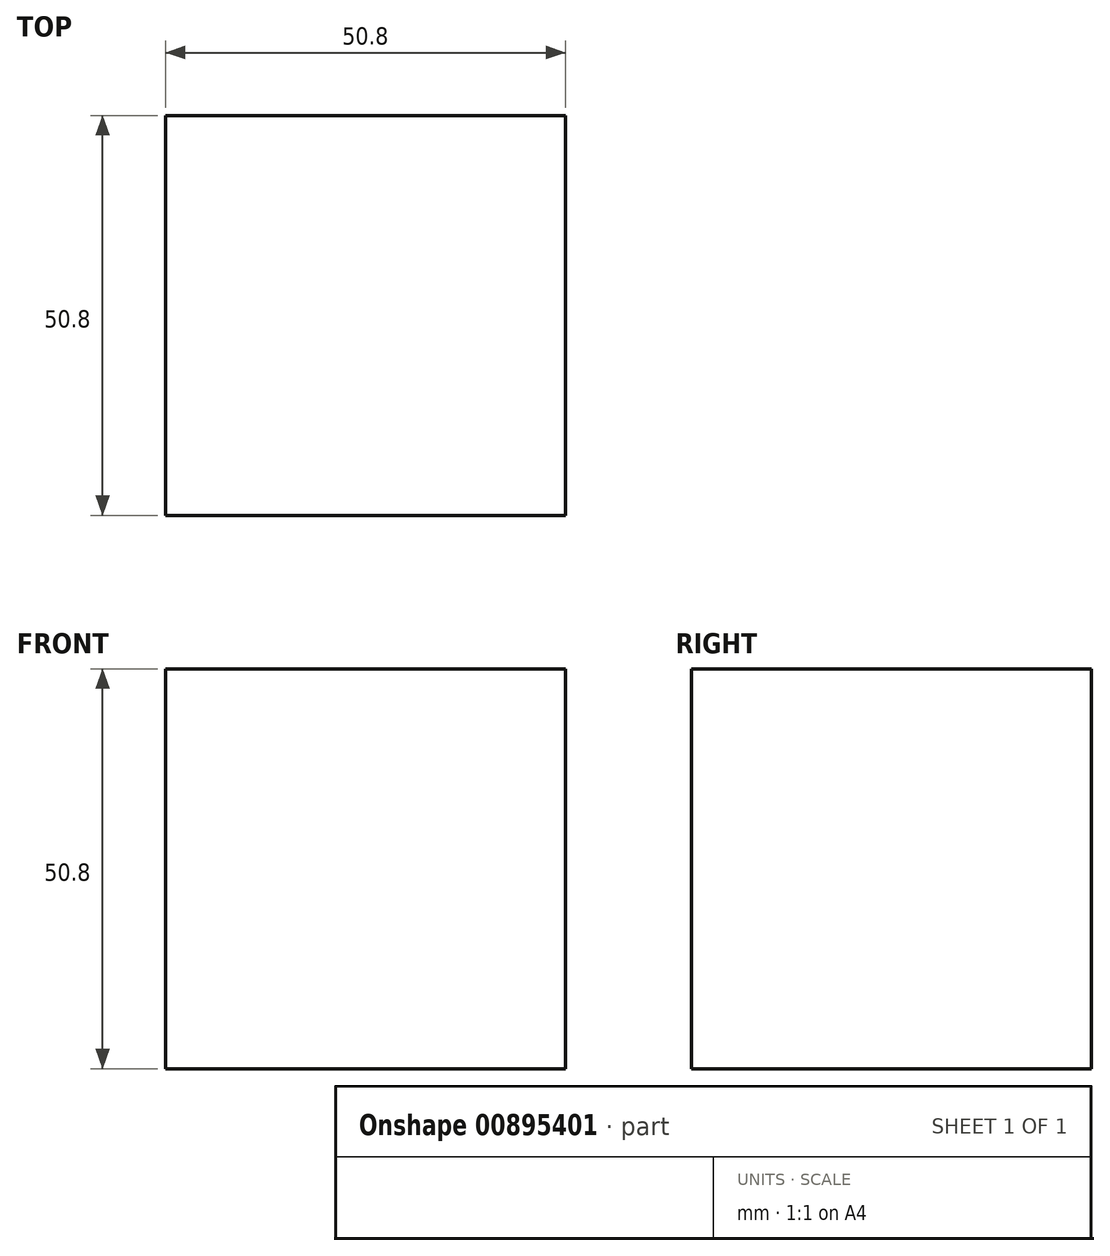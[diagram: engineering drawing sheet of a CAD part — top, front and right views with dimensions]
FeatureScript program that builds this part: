
annotation { "Feature Type Name" : "Feature", "Feature Type Description" : "" }
export const myFeature = defineFeature(function(context is Context, id is Id, definition is map)
    precondition{}
    {
        {
            var Q0;
            Q0=qCreatedBy(makeId("Front.planeOp"),FACE);
            var sketch = newSketch(context, id + "F0", { "sketchPlane" : qUnion([Q0])});
            skLineSegment(sketch, "E0.bottom", {"start": v(25.4, 25.4) * mm, "end": v(-25.4, 25.4) * mm});
            skLineSegment(sketch, "E0.top", {"start": v(25.4, -25.4) * mm, "end": v(-25.4, -25.4) * mm});
            skLineSegment(sketch, "E0.left", {"start": v(25.4, 25.4) * mm, "end": v(25.4, -25.4) * mm});
            skLineSegment(sketch, "E0.right", {"start": v(-25.4, 25.4) * mm, "end": v(-25.4, -25.4) * mm});
            skPoint(sketch, "E0.middle", {"position": v(0, 0) * mm});
            skSolve(sketch);
        }
        {
            var Q0;
            Q0 = qSketchRegion(id + "F0", true);
            extrude(context, id + "F1", {"entities" : qUnion([Q0]), "depth" : 50.8 * mm, "offsetDistance" : 25.4 * mm});
        }
    });
